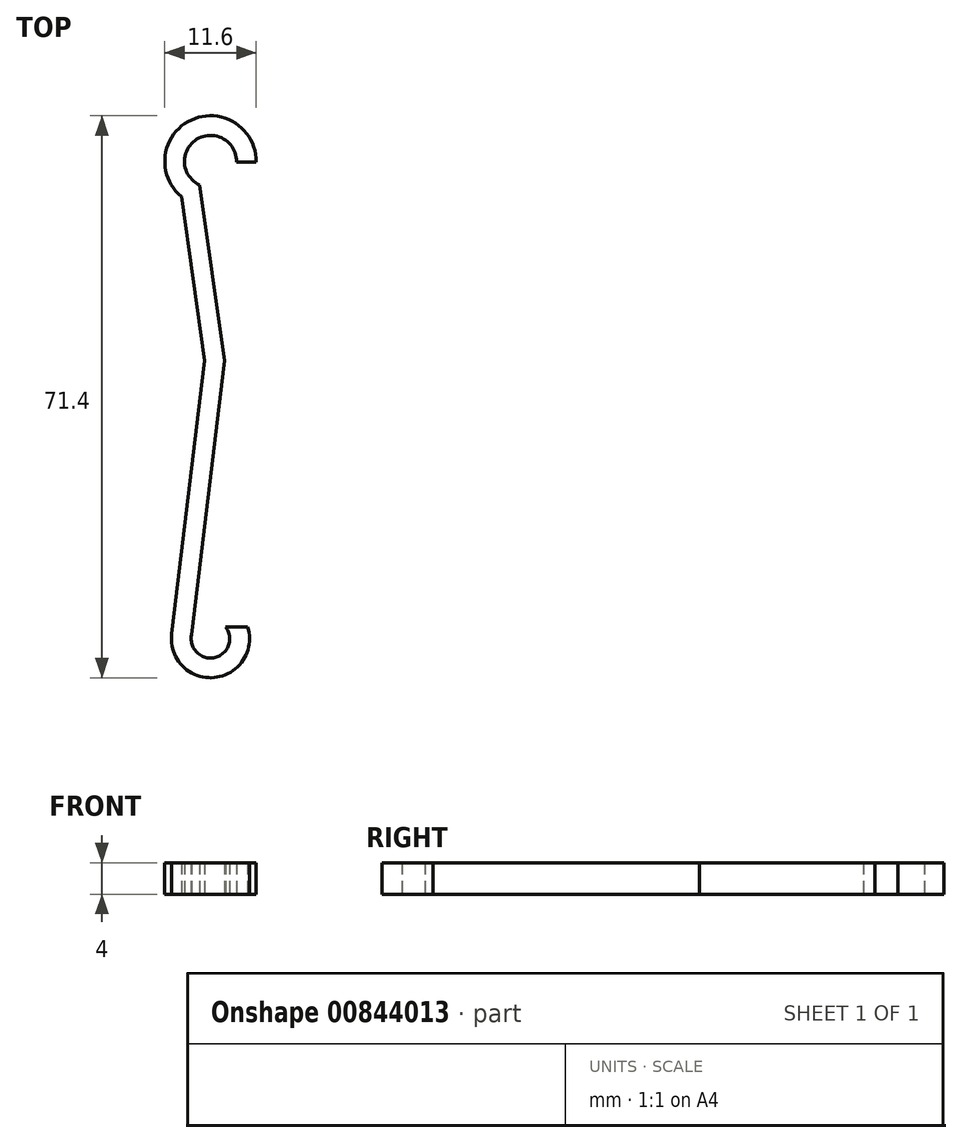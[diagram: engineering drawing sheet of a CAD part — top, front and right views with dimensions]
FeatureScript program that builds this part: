
annotation { "Feature Type Name" : "Feature", "Feature Type Description" : "" }
export const myFeature = defineFeature(function(context is Context, id is Id, definition is map)
    precondition{}
    {
        {
            var Q0;
            Q0=qCreatedBy(makeId("Top.planeOp"),FACE);
            var sketch = newSketch(context, id + "F0", { "sketchPlane" : qUnion([Q0])});
            skArc(sketch, "E0", {"start": v(3.3, 10) * mm, "mid": v(-1.74, 12.9) * mm, "end": v(-1.37, 7.1) * mm});
            skArc(sketch, "E1.0", {"start": v(5.8, 10) * mm, "mid": v(-2.43, 15.37) * mm, "end": v(-3.69, 5.62) * mm});
            skLineSegment(sketch, "E2", {"start": v(3.3, 10) * mm, "end": v(5.8, 10) * mm});
            skLineSegment(sketch, "E3", {"start": v(-1.37, 7.1) * mm, "end": v(1.8, -15.2) * mm});
            skLineSegment(sketch, "E4", {"start": v(1.8, -15.2) * mm, "end": v(-2.4, -50.07) * mm});
            skArc(sketch, "E5", {"start": v(-2.4, -50.07) * mm, "mid": v(0.56, -52.93) * mm, "end": v(1.94, -49.05) * mm});
            skLineSegment(sketch, "E6", {"start": v(-3.69, 5.62) * mm, "end": v(-0.72, -15.2) * mm});
            skLineSegment(sketch, "E7", {"start": v(-0.72, -15.2) * mm, "end": v(-4.91, -49.96) * mm});
            skArc(sketch, "E8", {"start": v(-4.91, -49.96) * mm, "mid": v(0.46, -55.48) * mm, "end": v(4.72, -49.05) * mm});
            skLineSegment(sketch, "E9", {"start": v(1.94, -49.05) * mm, "end": v(4.72, -49.05) * mm});
            skSolve(sketch);
        }
        {
            var Q0;
            Q0=makeQuery(id+"F0.imprint","IMPRINT",FACE,{"disambiguationData":[TD([[makeQuery(id+"F0.imprint","IMPRINT",EDGE,{"derivedFrom":sQuery(id+"F0.wireOp",EDGE,"E0")}),-1.0]])]});
            extrude(context, id + "F1", {"entities" : qUnion([Q0]), "depth" : 4 * mm, "offsetDistance" : 25 * mm});
        }
    });
